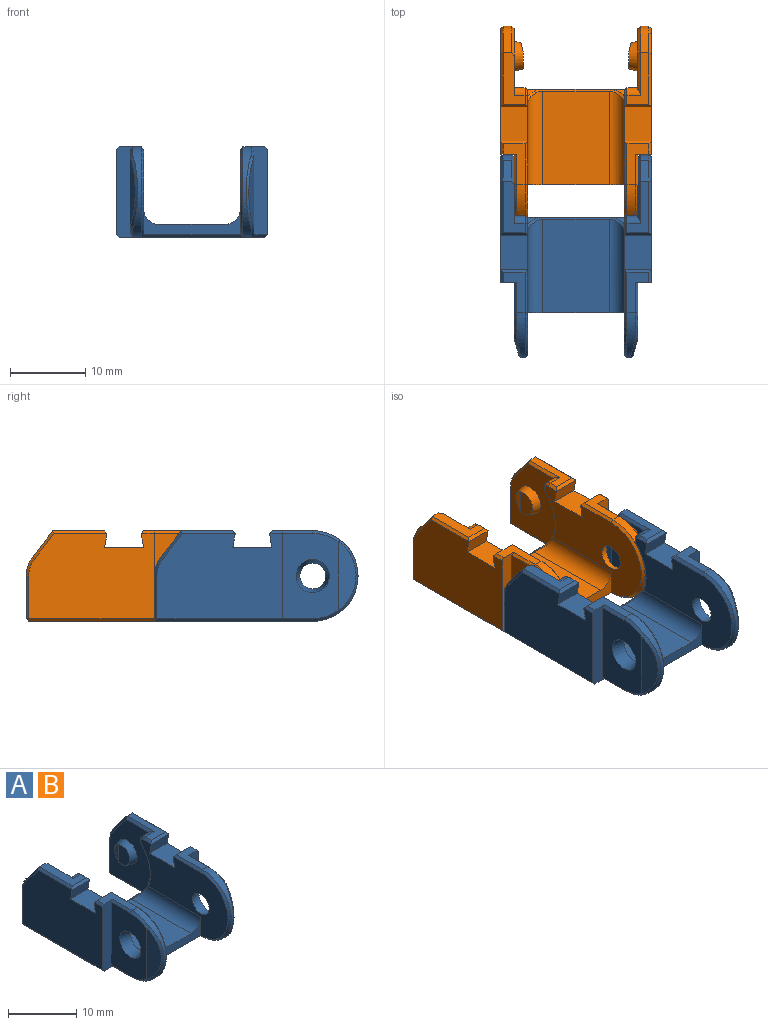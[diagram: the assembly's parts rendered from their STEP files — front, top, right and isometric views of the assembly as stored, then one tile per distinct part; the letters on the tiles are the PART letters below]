
ASSEMBLY  parts=2 mates=1
PART A: 107 faces, bbox 20.2x27.2x12.2 mm
  f0: cylinder r=6.2mm len=8.69mm, axis (1,0,0), area 16.7mm2, adj f9,f38,f40,f87,f89
  f1: plane 5.38x2.9mm, normal (0,0,1), area 8.4mm2, adj f3,f12,f48,f104,f105,f106
  f2: plane 11.3x7.36mm, normal (1,0,0), area 65.5mm2, adj f12,f18,f21,f48,f50,f54,f60
  f3: cylinder r=6mm len=12mm, axis (-1,0,0), area 15.9mm2, adj f1,f8,f50,f53,f54,f103
  f4: cone r=2mm half-angle=15deg, axis (1,0,0), area 13.5mm2, adj f5,f17,f20
  f5: plane 3.36x2.28mm, normal (-1,0,0), area 6.4mm2, adj f4,f20
  f6: plane 12.39x8.8mm, normal (0,0,1), area 109mm2, adj f7,f46,f47,f90
  f7: plane 12.8x3.35mm, normal (0,-1,0), area 19mm2, adj f6,f11,f32,f46,f47,f101
  f8: plane 20.65x19.3mm, normal (0,0,-1), area 235.5mm2, adj f3,f27,f33,f56,f59,f60,f61,f64
  f9: plane 16.41x1.28mm, normal (0,1,0), area 20.7mm2, adj f0,f17,f30,f38,f56,f88,f89,f90
  f10: plane 6.82x2.9mm, normal (0,0,1), area 9.7mm2, adj f15,f19,f49,f78,f80,f82
  f11: plane 18.12x11.3mm, normal (-1,0,0), area 120mm2, adj f7,f18,f22,f23,f24,f46,f80,f82
  f12: plane 11.65x2.15mm, normal (0,-1,0), area 21mm2, adj f1,f2,f16,f48,f64,f105
  f13: plane 5.65x1.1mm, normal (0,1,0), area 6.2mm2, adj f14,f58,f66,f72
  f14: cylinder r=4mm len=2.44mm, axis (-1,0,0), area 2.9mm2, adj f13,f15,f55,f74
  f15: plane 3.57x2.74mm, normal (0,0.79,0.61), area 5mm2, adj f10,f14,f51,f76
  f16: plane 16.65x11.3mm, normal (1,0,0), area 171.6mm2, adj f12,f22,f23,f24,f67,f72,f74,f76
  f17: plane 11.3x9.85mm, normal (-1,0,0), area 81.4mm2, adj f4,f9,f19,f30,f49,f51,f55,f58
  f18: cone r=2.19mm half-angle=15deg, axis (1,0,0), area 23mm2, adj f2,f11
  f19: cylinder r=1mm len=1.8mm, axis (-1,0,0), area 3.5mm2, adj f10,f17,f30,f49,f84
  f20: plane 3.13x1.16mm, normal (-0.97,0.25,0), area 2.8mm2, adj f4,f5
  f21: plane 9.1x2.4mm, normal (0.96,-0.27,0), area 16mm2, adj f2,f50,f53,f54
  f22: plane 3.6x1.79mm, normal (0,0.99,-0.17), area 6.5mm2, adj f11,f16,f24,f106
  f23: plane 3.6x1.79mm, normal (0,-0.99,-0.17), area 6.5mm2, adj f11,f16,f24,f80
  f24: plane 5.18x3.6mm, normal (0,0,1), area 18.6mm2, adj f11,f16,f22,f23
  f25: plane 5.38x2.9mm, normal (0,0,1), area 8.4mm2, adj f27,f33,f95,f96,f97,f98
  f26: plane 11.3x7.36mm, normal (-1,0,0), area 65.5mm2, adj f33,f39,f42,f91,f92,f94,f95
  f27: cylinder r=6mm len=12mm, axis (1,0,0), area 15.9mm2, adj f8,f25,f92,f93,f94,f99
  f28: cone r=2mm half-angle=15deg, axis (-1,0,0), area 13.5mm2, adj f29,f38,f41
  f29: plane 3.36x2.28mm, normal (1,0,0), area 6.4mm2, adj f28,f41
  f30: cylinder r=6.2mm len=8.69mm, axis (1,0,0), area 16.7mm2, adj f9,f17,f19,f86,f88
  f31: plane 6.82x2.9mm, normal (0,0,1), area 11.6mm2, adj f36,f38,f40,f52,f79,f81,f83
  f32: plane 18.12x11.3mm, normal (1,0,0), area 120mm2, adj f7,f39,f43,f44,f45,f47,f81,f83
  f33: plane 12x2.15mm, normal (0,-1,0), area 21.6mm2, adj f8,f25,f26,f37,f68,f91,f95,f96
  f34: plane 5.65x1.1mm, normal (0,1,0), area 6.2mm2, adj f35,f62,f69,f73
  f35: cylinder r=4mm len=2.44mm, axis (1,0,0), area 2.9mm2, adj f34,f36,f57,f75
  f36: plane 3.57x2.74mm, normal (0,0.79,0.61), area 5mm2, adj f31,f35,f52,f77
  f37: plane 16.65x11.3mm, normal (-1,0,0), area 171.6mm2, adj f33,f43,f44,f45,f68,f73,f75,f77
  f38: plane 11.65x9.85mm, normal (1,0,0), area 83.1mm2, adj f0,f9,f28,f31,f40,f52,f57,f61
  f39: cone r=2.19mm half-angle=15deg, axis (-1,0,0), area 23mm2, adj f26,f32
  f40: cylinder r=1mm len=1.69mm, axis (1,0,0), area 3.4mm2, adj f0,f31,f38,f85
  f41: plane 3.13x1.16mm, normal (0.97,0.25,0), area 2.8mm2, adj f28,f29
  f42: plane 9.1x2.4mm, normal (-0.96,-0.27,0), area 16mm2, adj f26,f92,f93,f94
  f43: plane 3.6x1.79mm, normal (0,0.99,-0.17), area 6.5mm2, adj f32,f37,f45,f97
  f44: plane 3.6x1.79mm, normal (0,-0.99,-0.17), area 6.5mm2, adj f32,f37,f45,f81
  f45: plane 5.18x3.6mm, normal (0,0,1), area 18.6mm2, adj f32,f37,f43,f44
  f46: cylinder r=2mm len=12.39mm, axis (0,1,0), area 36.5mm2, adj f6,f7,f11,f88
  f47: cylinder r=2mm len=12.39mm, axis (0,1,0), area 36.5mm2, adj f6,f7,f32,f89
  f48: plane 4x0.35mm, normal (0.71,0,0.71), area 2mm2, adj f1,f2,f12,f50
  f49: plane 5.78x0.52mm, normal (-0.71,0,0.71), area 2.5mm2, adj f10,f17,f19,f51
  f50: cone r=5.65mm half-angle=45deg, axis (-1,0,0), area 1.9mm2, adj f2,f3,f21,f48,f53
  f51: plane 3.78x2.91mm, normal (-0.71,0.56,0.43), area 2.2mm2, adj f15,f17,f49,f55
  f52: plane 3.78x3.18mm, normal (0.71,0.56,0.43), area 2.3mm2, adj f31,f36,f38,f57
  f53: bspline ~9.72x2.59mm, area 4.7mm2, adj f3,f21,f50,f54
  f54: cone r=5.65mm half-angle=45deg, axis (-1,0,0), area 1.9mm2, adj f2,f3,f21,f53,f60
  f55: cone r=4mm half-angle=45deg, axis (1,0,0), area 1.2mm2, adj f14,f17,f51,f58
  f56: plane 17.1x0.35mm, normal (0,0.71,-0.71), area 8.3mm2, adj f8,f9,f59,f61
  f57: cone r=3.65mm half-angle=45deg, axis (-1,0,0), area 1.2mm2, adj f35,f38,f52,f62
  f58: plane 5.65x0.35mm, normal (-0.71,0.71,0), area 2.8mm2, adj f13,f17,f55,f63
  f59: plane 8.38x0.35mm, normal (-0.71,0,-0.71), area 4.1mm2, adj f8,f17,f56,f63
  f60: plane 4.35x0.35mm, normal (0.71,0,-0.71), area 2.1mm2, adj f2,f8,f54,f64
  f61: plane 8.38x0.35mm, normal (0.71,0,-0.71), area 4.1mm2, adj f8,f38,f56,f65
  f62: plane 5.65x0.35mm, normal (0.71,0.71,0), area 2.8mm2, adj f34,f38,f57,f65
  f63: plane 0.35x0.35mm, normal (-0.58,0.58,-0.58), area 0.1mm2, adj f58,f59,f66
  f64: plane 2.15x0.35mm, normal (0,-0.71,-0.71), area 0.9mm2, adj f8,f12,f60,f67
  f65: plane 0.35x0.35mm, normal (0.58,0.58,-0.58), area 0.1mm2, adj f61,f62,f69
  f66: plane 1.1x0.35mm, normal (0,0.71,-0.71), area 0.5mm2, adj f8,f13,f63,f70
  f67: plane 16.65x0.35mm, normal (0.71,0,-0.71), area 8.1mm2, adj f8,f16,f64,f70
  f68: plane 16.65x0.35mm, normal (-0.71,0,-0.71), area 8.2mm2, adj f8,f33,f37,f71
  f69: plane 1.1x0.35mm, normal (0,0.71,-0.71), area 0.5mm2, adj f8,f34,f65,f71
  f70: plane 0.35x0.35mm, normal (0.58,0.58,-0.58), area 0.1mm2, adj f66,f67,f72
  f71: plane 0.35x0.35mm, normal (-0.58,0.58,-0.58), area 0.1mm2, adj f68,f69,f73
  f72: plane 5.65x0.35mm, normal (0.71,0.71,0), area 2.8mm2, adj f13,f16,f70,f74
  f73: plane 5.65x0.35mm, normal (-0.71,0.71,0), area 2.8mm2, adj f34,f37,f71,f75
  f74: cone r=3.65mm half-angle=45deg, axis (-1,0,0), area 1.2mm2, adj f14,f16,f72,f76
  f75: cone r=4mm half-angle=45deg, axis (1,0,0), area 1.2mm2, adj f35,f37,f73,f77
  f76: plane 3.78x2.91mm, normal (0.71,0.56,0.43), area 2.2mm2, adj f15,f16,f74,f78
  f77: plane 3.78x2.91mm, normal (-0.71,0.56,0.43), area 2.2mm2, adj f36,f37,f75,f79
  f78: plane 7.11x0.35mm, normal (0.71,0,0.71), area 3.4mm2, adj f10,f16,f76,f80
  f79: plane 7.11x0.35mm, normal (-0.71,0,0.71), area 3.4mm2, adj f31,f37,f77,f81
  f80: plane 3.6x0.41mm, normal (0,-0.77,0.64), area 1.8mm2, adj f10,f11,f16,f23,f78,f82
  f81: plane 3.6x0.41mm, normal (0,-0.77,0.64), area 1.8mm2, adj f31,f32,f37,f44,f79,f83
  f82: plane 1.49x0.35mm, normal (-0.71,0,0.71), area 0.7mm2, adj f10,f11,f80,f84
  f83: plane 1.49x0.35mm, normal (0.71,0,0.71), area 0.7mm2, adj f31,f32,f81,f85
  f84: cone r=0.65mm half-angle=45deg, axis (1,0,0), area 1mm2, adj f11,f19,f82,f86
  f85: cone r=1mm half-angle=45deg, axis (-1,0,0), area 1mm2, adj f32,f40,f83,f87
  f86: cone r=6.55mm half-angle=45deg, axis (-1,0,0), area 3.5mm2, adj f11,f30,f84,f88
  f87: cone r=6.2mm half-angle=45deg, axis (1,0,0), area 3.5mm2, adj f0,f32,f85,f89
  f88: bspline ~2.35x2.22mm, area 1.4mm2, adj f9,f30,f46,f86,f90
  f89: bspline ~2.35x2.22mm, area 1.4mm2, adj f0,f9,f47,f87,f90
  f90: plane 8.8x0.23mm, normal (0,0.38,0.92), area 2.2mm2, adj f6,f9,f88,f89
  f91: plane 4x0.35mm, normal (-0.71,0,-0.71), area 2mm2, adj f8,f26,f33,f92
  f92: cone r=6mm half-angle=45deg, axis (1,0,0), area 1.9mm2, adj f26,f27,f42,f91,f93
  f93: bspline ~9.72x2.59mm, area 4.7mm2, adj f27,f42,f92,f94
  f94: cone r=6mm half-angle=45deg, axis (1,0,0), area 1.9mm2, adj f26,f27,f42,f93,f95
  f95: plane 4x0.35mm, normal (-0.71,0,0.71), area 2mm2, adj f25,f26,f33,f94
  f96: plane 1.68x0.35mm, normal (-0.71,0,0.71), area 0.8mm2, adj f25,f33,f37,f97
  f97: plane 3.6x0.41mm, normal (0,0.77,0.64), area 1.8mm2, adj f25,f32,f37,f43,f96,f98
  f98: plane 5.68x0.35mm, normal (0.71,0,0.71), area 2.7mm2, adj f25,f32,f97,f99
  f99: cone r=5.65mm half-angle=45deg, axis (-1,0,0), area 9mm2, adj f27,f32,f98,f100
  f100: plane 0.35x0.35mm, normal (0.71,0,-0.71), area 0.1mm2, adj f8,f99,f101
  f101: plane 13.5x0.35mm, normal (0,-0.71,-0.71), area 6.5mm2, adj f7,f8,f100,f102
  f102: plane 0.35x0.35mm, normal (-0.71,0,-0.71), area 0.1mm2, adj f8,f101,f103
  f103: cone r=6mm half-angle=45deg, axis (1,0,0), area 9mm2, adj f3,f11,f102,f104
  f104: plane 5.68x0.35mm, normal (-0.71,0,0.71), area 2.7mm2, adj f1,f11,f103,f106
  f105: plane 1.68x0.35mm, normal (0.71,0,0.71), area 0.8mm2, adj f1,f12,f16,f106
  f106: plane 3.6x0.41mm, normal (0,0.77,0.64), area 1.8mm2, adj f1,f11,f16,f22,f104,f105
PART B: same geometry as A
PLACE A t=(-1.44,20.97,-12.68)mm fixed
PLACE B t=(-1.44,37.97,-12.68)mm
MATE revolute B.f3 <-> A.f0  axis (-1,0,0) through (-9.64,24.97,-6.68)mm
